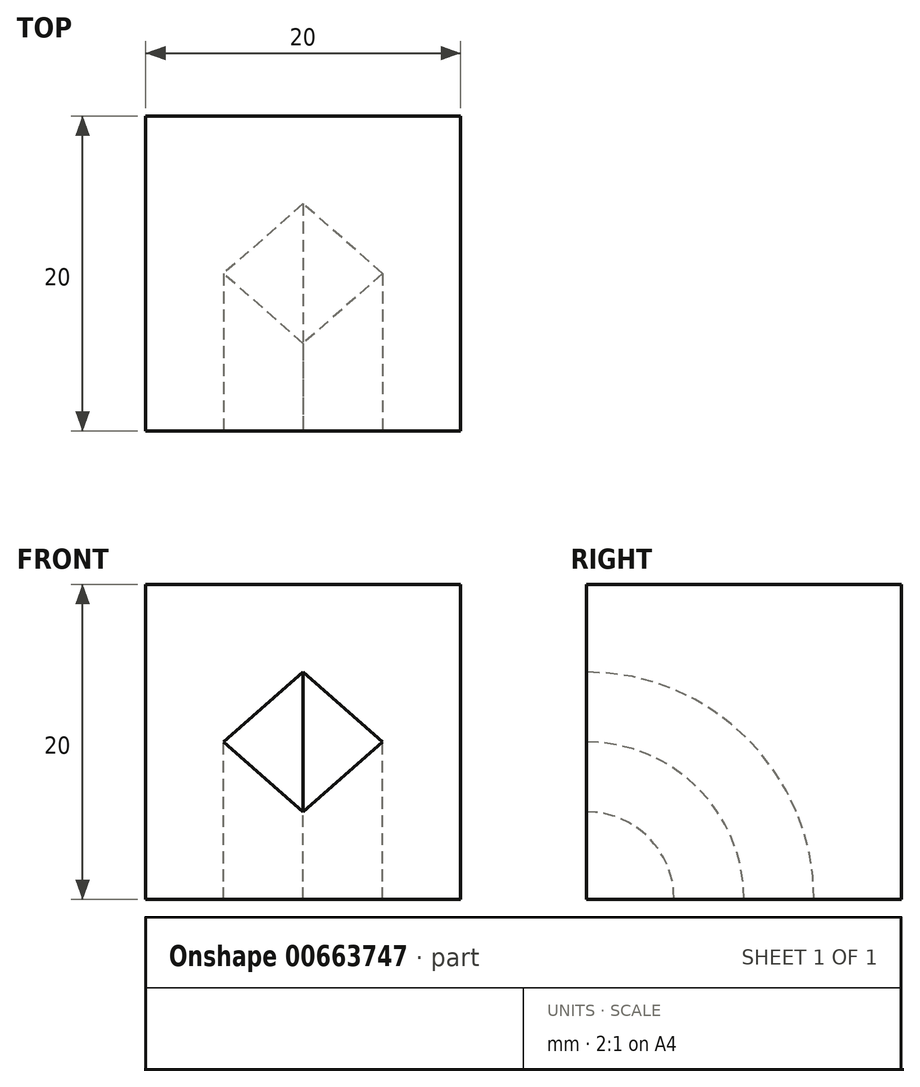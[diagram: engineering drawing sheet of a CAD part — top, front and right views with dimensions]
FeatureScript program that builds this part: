
annotation { "Feature Type Name" : "Feature", "Feature Type Description" : "" }
export const myFeature = defineFeature(function(context is Context, id is Id, definition is map)
    precondition{}
    {
        {
            assignVariable(context, id + "F0", {"name" : "size", "anyValue" : 20});
        }
        {
            var Q0;
            Q0=qCreatedBy(makeId("Front.planeOp"),FACE);
            var sketch = newSketch(context, id + "F1", { "sketchPlane" : qUnion([Q0])});
            skLineSegment(sketch, "E0.bottom", {"start": v(0, 0) * mm, "end": v(0, 0) * mm});
            skLineSegment(sketch, "E0.top", {"start": v(0, 0) * mm, "end": v(0, 0) * mm});
            skLineSegment(sketch, "E0.left", {"start": v(0, 0) * mm, "end": v(0, 0) * mm});
            skLineSegment(sketch, "E0.right", {"start": v(0, 0) * mm, "end": v(0, 0) * mm});
            skPoint(sketch, "E0.middle", {"position": v(0, 0) * mm});
            skLineSegment(sketch, "E1.bottom", {"start": v(-10, 10) * mm, "end": v(10, 10) * mm});
            skLineSegment(sketch, "E1.top", {"start": v(-10, -10) * mm, "end": v(10, -10) * mm});
            skLineSegment(sketch, "E1.left", {"start": v(-10, 10) * mm, "end": v(-10, -10) * mm});
            skLineSegment(sketch, "E1.right", {"start": v(10, 10) * mm, "end": v(10, -10) * mm});
            skSolve(sketch);
        }
        {
            var Q0;
            Q0=makeQuery(id+"F1.imprint","IMPRINT",FACE,{"disambiguationData":[TD([[makeQuery(id+"F1.imprint","IMPRINT",EDGE,{"derivedFrom":sQuery(id+"F1.wireOp",EDGE,"E1.bottom")}),-1.0]])]});
            extrude(context, id + "F2", {"entities" : qUnion([Q0]), "depth" : (getVariable(context, 'size')) * mm, "offsetDistance" : 25 * mm});
        }
        {
            var Q0;
            Q0=makeQuery(id+"F2.opExtrude","CAP_FACE",FACE,{"disambiguationData":[OSD([sQuery(id+"F1.wireOp",EDGE,"E1.bottom"),sQuery(id+"F1.wireOp",EDGE,"E1.top"),sQuery(id+"F1.wireOp",EDGE,"E1.left"),sQuery(id+"F1.wireOp",EDGE,"E1.right")])],"isStart":false});
            var sketch = newSketch(context, id + "F3", { "sketchPlane" : qUnion([Q0])});
            skLineSegment(sketch, "E2", {"start": v(-5.05, 0) * mm, "end": v(0, 4.44) * mm});
            skLineSegment(sketch, "E3", {"start": v(0, 4.44) * mm, "end": v(5.05, 0) * mm});
            skLineSegment(sketch, "E4", {"start": v(5.05, 0) * mm, "end": v(0, -4.44) * mm});
            skLineSegment(sketch, "E5", {"start": v(0, -4.44) * mm, "end": v(-5.05, 0) * mm});
            skSolve(sketch);
        }
        {
            var Q0;
            Q0=makeQuery(id+"F3.imprint","IMPRINT",FACE,{"disambiguationData":[TD([[makeQuery(id+"F3.imprint","IMPRINT",EDGE,{"derivedFrom":sQuery(id+"F3.wireOp",EDGE,"E2")}),-1.0]])]});
            var Q1;
            Q1=makeQuery(id+"F2.opExtrude","CAP_EDGE",EDGE,{"disambiguationData":[OSD([sQuery(id+"F1.wireOp",EDGE,"E1.top")])],"isStart":false});
            revolve(context, id + "F4", {"operationType" : NewBodyOperationType.REMOVE, "entities" : qUnion([Q0]), "axis" : qUnion([Q1]), "revolveType" : RevolveType.FULL, "oppositeDirection" : true});
        }
    });
